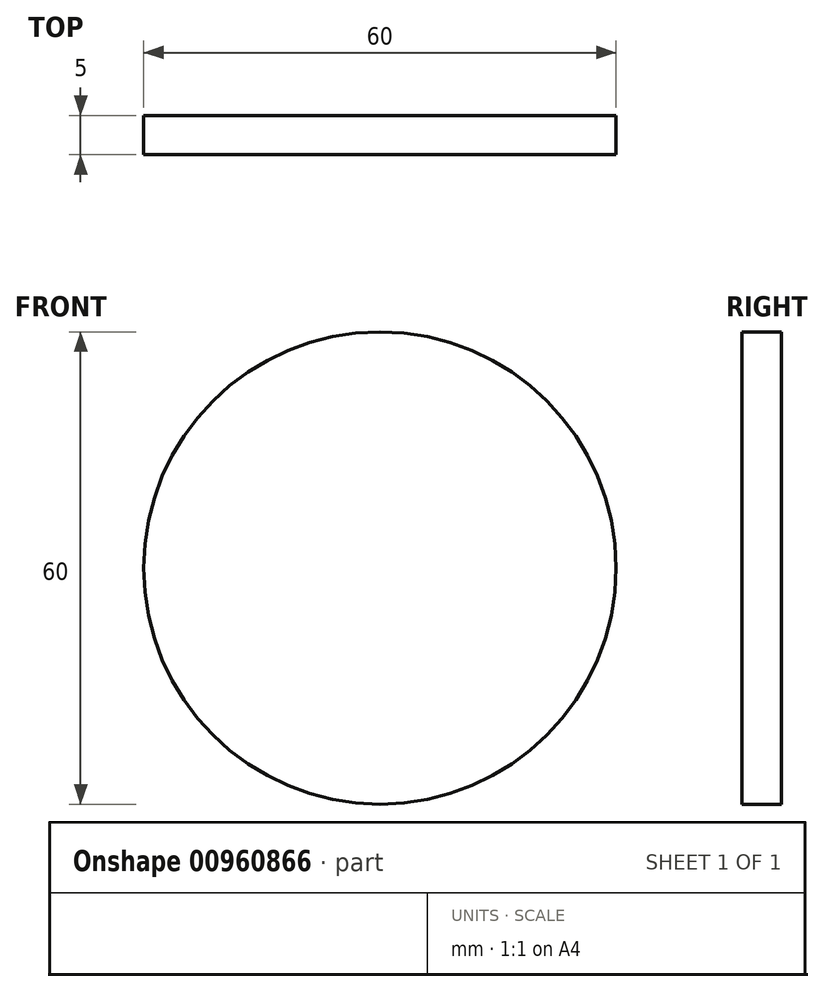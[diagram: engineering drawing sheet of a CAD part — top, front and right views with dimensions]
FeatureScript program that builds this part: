
annotation { "Feature Type Name" : "Feature", "Feature Type Description" : "" }
export const myFeature = defineFeature(function(context is Context, id is Id, definition is map)
    precondition{}
    {
        {
            var Q0;
            Q0=qCreatedBy(makeId("Front.planeOp"),FACE);
            var sketch = newSketch(context, id + "F0", { "sketchPlane" : qUnion([Q0])});
            skCircle(sketch, "E0", {"center": v(0, 0) * mm, "radius": 30 * mm});
            skSolve(sketch);
        }
        {
            var Q0;
            Q0=makeQuery(id+"F0.imprint","IMPRINT",FACE,{"disambiguationData":[TD([[makeQuery(id+"F0.imprint","IMPRINT",EDGE,{"derivedFrom":sQuery(id+"F0.wireOp",EDGE,"E0")}),1.0]])]});
            extrude(context, id + "F1", {"entities" : qUnion([Q0]), "depth" : 5 * mm, "offsetDistance" : 25 * mm});
        }
    });
